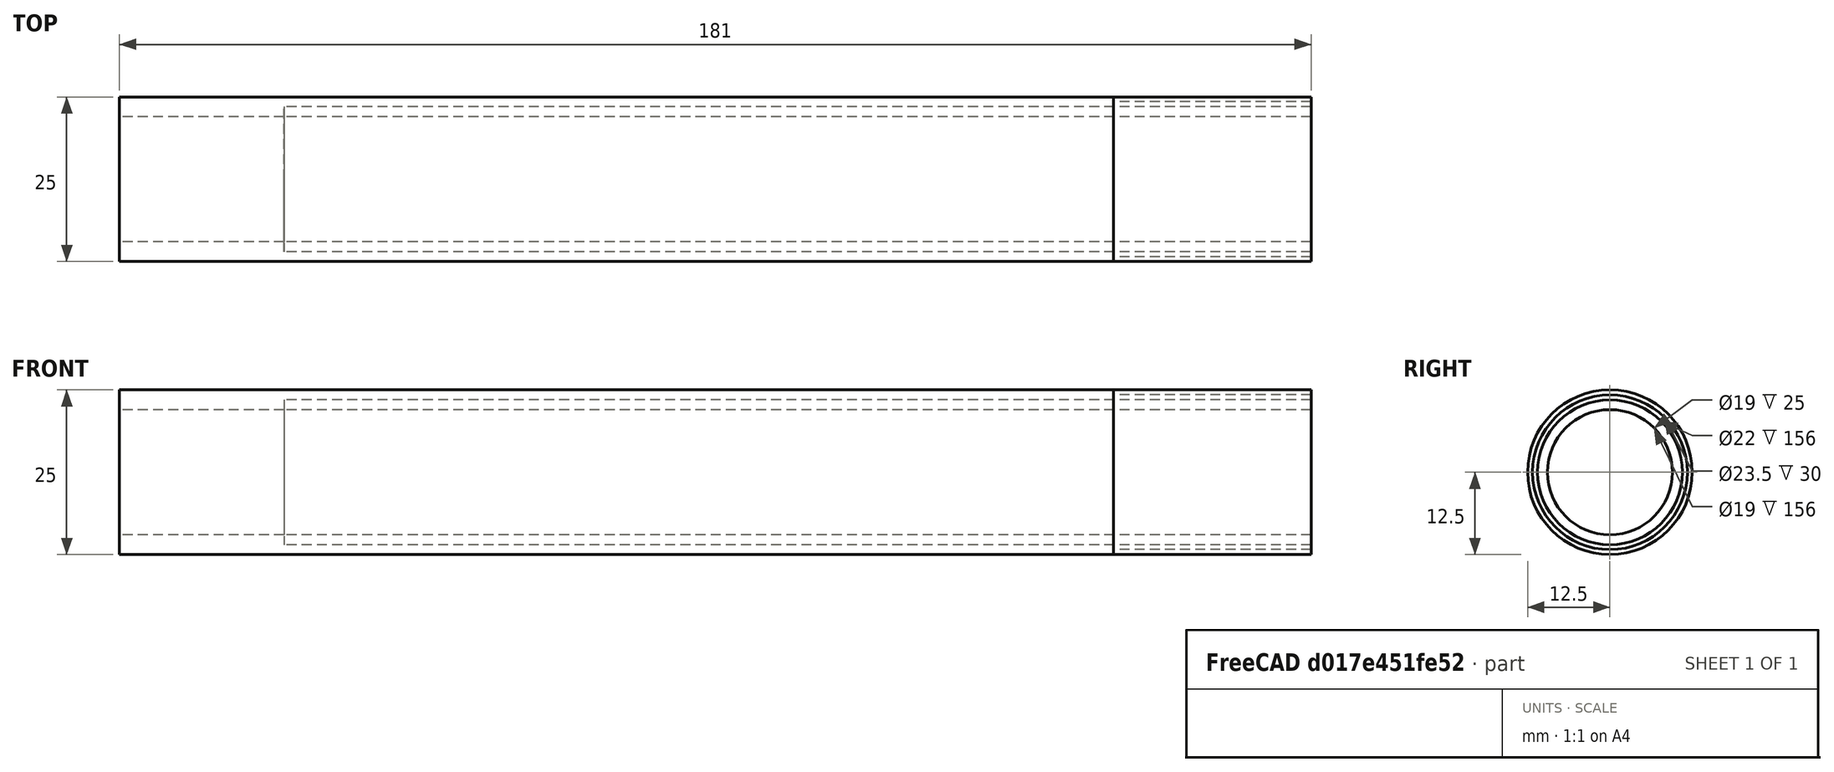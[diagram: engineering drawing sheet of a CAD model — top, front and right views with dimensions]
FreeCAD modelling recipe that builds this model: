
FCSTD DOCUMENT  (FreeCAD 0.16R)
Label: model1
License: All rights reserved
LicenseURL: http://en.wikipedia.org/wiki/All_rights_reserved
objects: Part::Cylinder×7, Part::Cut×4, App::FeaturePython×3, Drawing::FeatureViewPart×1, Drawing::FeaturePage×1
note: 11 computed .brp shape members not serialized (recipe doc carries the construction recipe); baked Part::Feature solids carry a one-line shape summary decoded from their .brp

FEATURE [Part::Cylinder] Cylinder  label="ExtC"
  Angle = 360
  Height = 156
  Placement = pos=(0,0,0) rot=(0,-1,0;1.5708rad)
  Radius = 11
FEATURE [Part::Cylinder] Cylinder001  label="InnerC"
  Angle = 360
  Height = 156
  Placement = pos=(0,0,0) rot=(0,-1,0;1.5708rad)
  Radius = 9.5
FEATURE [Part::Cut] Cut  label="SteelTube"
  Base = -> Cylinder
  Tool = -> Cylinder001
FEATURE [Part::Cylinder] Cylinder002  label="Цилиндр"
  Angle = 360
  Height = 181
  Placement = pos=(0,0,0) rot=(0,-1,0;1.5708rad)
  Radius = 12.5
FEATURE [Part::Cylinder] Cylinder003  label="Цилиндр001"
  Angle = 360
  Height = 156
  Placement = pos=(0,0,0) rot=(0,-1,0;1.5708rad)
  Radius = 11
FEATURE [Part::Cylinder] Cylinder004  label="Цилиндр002"
  Angle = 360
  Height = 25
  Placement = pos=(-156,0,0) rot=(0,-1,0;1.5708rad)
  Radius = 9.5
FEATURE [Part::Cut] Cut001
  Base = -> Cylinder002
  Tool = -> Cylinder003
FEATURE [Part::Cut] Cut002  label="BatteryPart"
  Base = -> Cut001
  Tool = -> Cylinder004
FEATURE [Part::Cylinder] Cylinder005  label="Цилиндр003"
  Angle = 360
  Height = 30
  Placement = pos=(0,0,0) rot=(0,-1,0;1.5708rad)
  Radius = 12.5
FEATURE [Part::Cylinder] Cylinder006  label="Цилиндр004"
  Angle = 360
  Height = 30
  Placement = pos=(0,0,0) rot=(0,-1,0;1.5708rad)
  Radius = 11.75
FEATURE [Part::Cut] Cut003
  Base = -> Cylinder005
  Tool = -> Cylinder006
FEATURE [App::FeaturePython] Dimension  # Draft dimension (typed FeaturePython)
  Dimline = (0,-9.5,0)
  Direction = (0,0,0)
  Distance = 1.5
  End = (0,-9.5,0)
  Normal = (0,0,1)
  Start = (0,-11,0)
FEATURE [App::FeaturePython] Dimension001  # Draft dimension (typed FeaturePython)
  Dimline = (0,11,0)
  Direction = (0,0,0)
  Distance = 22
  End = (0,11,0)
  Normal = (0,0,1)
  Start = (0,-11,0)
FEATURE [App::FeaturePython] Dimension002  # Draft dimension (typed FeaturePython)
  Dimline = (0,9.5,0)
  Direction = (0,0,0)
  Distance = 19
  End = (0,9.5,0)
  Normal = (0,0,1)
  Start = (0,-9.5,0)
FEATURE [Drawing::FeatureViewPart] Ortho  label="Ortho_0_0"
  Direction = (1,0,0)
  HiddenWidth = 0.15
  LineWidth = 0.35
  Rotation = -90
  Scale = 5
  ShowHiddenLines = false
  ShowSmoothLines = false
  Source = -> Cut
  Tolerance = 0.05
  ViewResult = <g id="Ortho_0_0"\n   transform="rotate(-90,210,118.847) translate(210,118.847) scale(5,5)"\n  >\n<g   stroke="rgb(0, 0, 0)"\n   stroke-width="0.07"\n   stroke-linecap="butt"\n   stroke-linejoin="miter"\n   fill="none"\n   transform="scale(1,-1)"\n  >\n<circle cx ="0" cy ="0" r ="11" /><circle cx ="0" cy ="0" r ="9.5" /></g>\n</g>
  Visible = true
  X = 210
  Y = 118.847
FEATURE [Drawing::FeaturePage] Page
  EditableTexts = AUTHOR NAME | CREATION DATE | SUPERVISOR NAME | CHECK DATE | SCALE | WEIGHT | NUMBER | SHEET | TITLE | SUBTITLE
  Group = -> [Ortho]
